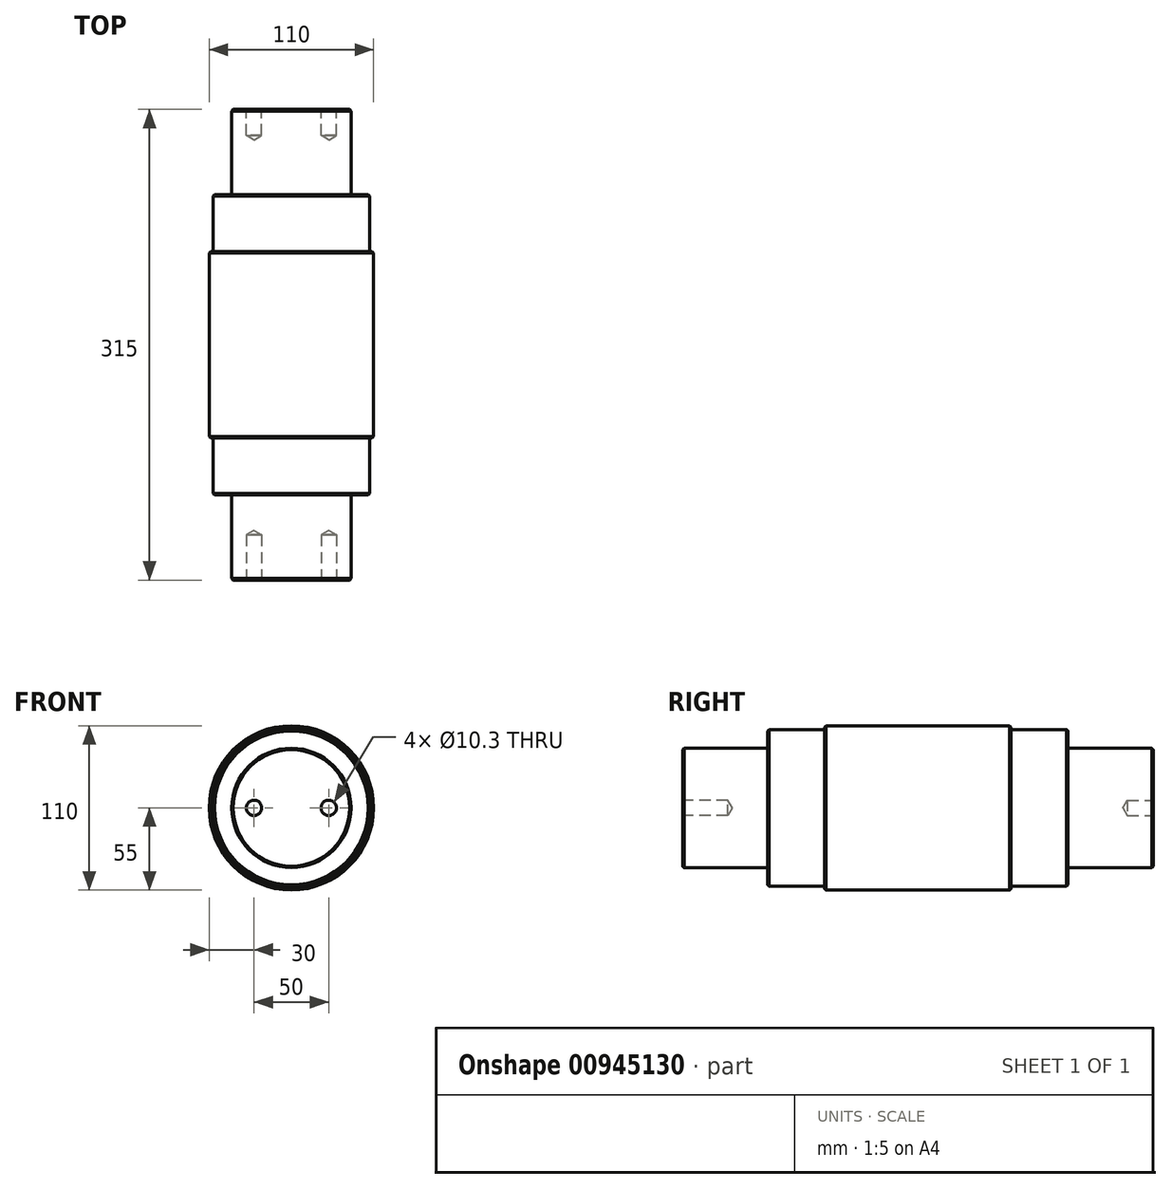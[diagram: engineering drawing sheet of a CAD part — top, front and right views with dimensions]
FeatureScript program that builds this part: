
annotation { "Feature Type Name" : "Feature", "Feature Type Description" : "" }
export const myFeature = defineFeature(function(context is Context, id is Id, definition is map)
    precondition{}
    {
        {
            var Q0;
            Q0=qCreatedBy(makeId("Front.planeOp"),FACE);
            var sketch = newSketch(context, id + "F0", { "sketchPlane" : qUnion([Q0])});
            skCircle(sketch, "E0", {"center": v(0, 0) * mm, "radius": 55 * mm});
            skSolve(sketch);
        }
        {
            var Q0;
            Q0=makeQuery(id+"F0.imprint","IMPRINT",FACE,{"disambiguationData":[TD([[makeQuery(id+"F0.imprint","IMPRINT",EDGE,{"derivedFrom":sQuery(id+"F0.wireOp",EDGE,"E0")}),1.0]])]});
            extrude(context, id + "F1", {"entities" : qUnion([Q0]), "oppositeDirection" : true, "depth" : 125 * mm, "offsetDistance" : 25 * mm});
        }
        {
            var Q0;
            Q0=makeQuery(id+"F1.opExtrude","CAP_FACE",FACE,{"disambiguationData":[OSD([sQuery(id+"F0.wireOp",EDGE,"E0")])],"isStart":true});
            var sketch = newSketch(context, id + "F2", { "sketchPlane" : qUnion([Q0])});
            skCircle(sketch, "E1", {"center": v(0, 0) * mm, "radius": 52.5 * mm});
            skSolve(sketch);
        }
        {
            var Q0;
            Q0=makeQuery(id+"F2.imprint","IMPRINT",FACE,{"disambiguationData":[TD([[makeQuery(id+"F2.imprint","IMPRINT",EDGE,{"derivedFrom":sQuery(id+"F2.wireOp",EDGE,"E1")}),1.0]])]});
            extrude(context, id + "F3", {"entities" : qUnion([Q0]), "operationType" : NewBodyOperationType.ADD, "depth" : 38 * mm, "offsetDistance" : 25 * mm});
        }
        {
            var Q0;
            Q0=makeQuery(id+"F3.opExtrude","CAP_FACE",FACE,{"disambiguationData":[OSD([sQuery(id+"F2.wireOp",EDGE,"E1")])],"isStart":false});
            var sketch = newSketch(context, id + "F4", { "sketchPlane" : qUnion([Q0])});
            skCircle(sketch, "E2", {"center": v(0, 0) * mm, "radius": 40 * mm});
            skSolve(sketch);
        }
        {
            var Q0;
            Q0=makeQuery(id+"F4.imprint","IMPRINT",FACE,{"disambiguationData":[TD([[makeQuery(id+"F4.imprint","IMPRINT",EDGE,{"derivedFrom":sQuery(id+"F4.wireOp",EDGE,"E2")}),1.0]])]});
            extrude(context, id + "F5", {"entities" : qUnion([Q0]), "operationType" : NewBodyOperationType.ADD, "depth" : 57 * mm, "offsetDistance" : 25 * mm});
        }
        {
            var Q0;
            Q0=makeQuery(id+"F1.opExtrude","CAP_FACE",FACE,{"disambiguationData":[OSD([sQuery(id+"F0.wireOp",EDGE,"E0")])],"isStart":false});
            var sketch = newSketch(context, id + "F6", { "sketchPlane" : qUnion([Q0])});
            skCircle(sketch, "E3", {"center": v(0, 0) * mm, "radius": 52.5 * mm});
            skSolve(sketch);
        }
        {
            var Q0;
            Q0=makeQuery(id+"F6.imprint","IMPRINT",FACE,{"disambiguationData":[TD([[makeQuery(id+"F6.imprint","IMPRINT",EDGE,{"derivedFrom":sQuery(id+"F6.wireOp",EDGE,"E3")}),1.0]])]});
            extrude(context, id + "F7", {"entities" : qUnion([Q0]), "operationType" : NewBodyOperationType.ADD, "depth" : 38 * mm, "offsetDistance" : 25 * mm});
        }
        {
            var Q0;
            Q0=makeQuery(id+"F7.opExtrude","CAP_FACE",FACE,{"disambiguationData":[OSD([sQuery(id+"F6.wireOp",EDGE,"E3")])],"isStart":false});
            var sketch = newSketch(context, id + "F8", { "sketchPlane" : qUnion([Q0])});
            skCircle(sketch, "E4", {"center": v(0, 0) * mm, "radius": 40 * mm});
            skSolve(sketch);
        }
        {
            var Q0;
            Q0=makeQuery(id+"F8.imprint","IMPRINT",FACE,{"disambiguationData":[TD([[makeQuery(id+"F8.imprint","IMPRINT",EDGE,{"derivedFrom":sQuery(id+"F8.wireOp",EDGE,"E4")}),1.0]])]});
            extrude(context, id + "F9", {"entities" : qUnion([Q0]), "operationType" : NewBodyOperationType.ADD, "depth" : 57 * mm, "offsetDistance" : 25 * mm});
        }
        {
            var Q0;
            Q0=makeQuery(id+"F5.opExtrude","CAP_EDGE",EDGE,{"disambiguationData":[OSD([sQuery(id+"F4.wireOp",EDGE,"E2")])],"isStart":false});
            chamfer(context, id + "F10", {"entities" : qUnion([Q0]), "width" : 1 * mm, "tangentPropagation" : true});
        }
        {
            var Q0;
            Q0=makeQuery(id+"F3.opExtrude","CAP_EDGE",EDGE,{"disambiguationData":[OSD([sQuery(id+"F2.wireOp",EDGE,"E1")])],"isStart":false});
            chamfer(context, id + "F11", {"entities" : qUnion([Q0]), "width" : 1 * mm, "tangentPropagation" : true});
        }
        {
            var Q0;
            Q0=makeQuery(id+"F1.opExtrude","CAP_EDGE",EDGE,{"disambiguationData":[OSD([sQuery(id+"F0.wireOp",EDGE,"E0")])],"isStart":true});
            chamfer(context, id + "F12", {"entities" : qUnion([Q0]), "width" : 1 * mm, "tangentPropagation" : true});
        }
        {
            var Q0;
            Q0=makeQuery(id+"F9.opExtrude","CAP_EDGE",EDGE,{"disambiguationData":[OSD([sQuery(id+"F8.wireOp",EDGE,"E4")])],"isStart":false});
            chamfer(context, id + "F13", {"entities" : qUnion([Q0]), "width" : 1 * mm, "tangentPropagation" : true});
        }
        {
            var Q0;
            Q0=makeQuery(id+"F7.opExtrude","CAP_EDGE",EDGE,{"disambiguationData":[OSD([sQuery(id+"F6.wireOp",EDGE,"E3")])],"isStart":false});
            chamfer(context, id + "F14", {"entities" : qUnion([Q0]), "width" : 1 * mm, "tangentPropagation" : true});
        }
        {
            var Q0;
            Q0=makeQuery(id+"F1.opExtrude","CAP_EDGE",EDGE,{"disambiguationData":[OSD([sQuery(id+"F0.wireOp",EDGE,"E0")])],"isStart":false});
            chamfer(context, id + "F15", {"entities" : qUnion([Q0]), "width" : 1 * mm, "tangentPropagation" : true});
        }
        {
            var Q0;
            Q0=makeQuery(id+"F5.opExtrude","CAP_FACE",FACE,{"disambiguationData":[OSD([sQuery(id+"F4.wireOp",EDGE,"E2")])],"isStart":false});
            var sketch = newSketch(context, id + "F16", { "sketchPlane" : qUnion([Q0])});
            skLineSegment(sketch, "E5", {"start": v(0, 0) * mm, "end": v(25, 0) * mm, "construction": true});
            skLineSegment(sketch, "E6", {"start": v(0, 0) * mm, "end": v(-25, 0) * mm, "construction": true});
            skSolve(sketch);
        }
        {
            var Q0;
            Q0=sQuery(id+"F16.wireOp",VERTEX,"E6.end");
            var Q1;
            Q1=sQuery(id+"F16.wireOp",VERTEX,"E5.end");
            var Q2;
            Q2=makeQuery(id+"F1.opExtrude","SWEPT_BODY",BODY,{"disambiguationData":[OSD([sQuery(id+"F0.wireOp",EDGE,"E0")])]});
            hole(context, id + "F17", {"style" : HoleStyle.SIMPLE, "endStyle" : HoleEndStyle.BLIND, "standardTappedOrClearance" : lookupTablePath({ "standard" : "ISO", "engagement" : "75%", "pitch" : "1.75 mm", "size" : "M12", "type" : "Tapped" }), "standardBlindInLast" : lookupTablePath({ "standard" : "ISO", "fit" : "Normal", "engagement" : "75%", "pitch" : "1.75 mm", "size" : "M12", "type" : "Clearance & tapped" }), "holeDiameter" : 10.3 * mm, "majorDiameter" : 12 * mm, "showTappedDepth" : true, "holeDepth" : 30.25 * mm, "isTappedThrough" : true, "tappedDepth" : 25 * mm, "tapClearance" : 3, "startFromSketch" : true, "locations" : qUnion([Q0, Q1]), "scope" : qUnion([Q2])});
        }
        {
            var Q0;
            Q0=makeQuery(id+"F9.opExtrude","CAP_FACE",FACE,{"disambiguationData":[OSD([sQuery(id+"F8.wireOp",EDGE,"E4")])],"isStart":false});
            var sketch = newSketch(context, id + "F18", { "sketchPlane" : qUnion([Q0])});
            skLineSegment(sketch, "E7", {"start": v(0, 0) * mm, "end": v(25, 0) * mm, "construction": true});
            skLineSegment(sketch, "E8", {"start": v(0, 0) * mm, "end": v(-25, 0) * mm, "construction": true});
            skSolve(sketch);
        }
        {
            var Q0;
            Q0=sQuery(id+"F18.wireOp",VERTEX,"E8.end");
            var Q1;
            Q1=sQuery(id+"F18.wireOp",VERTEX,"E7.end");
            var Q2;
            Q2=makeQuery(id+"F1.opExtrude","SWEPT_BODY",BODY,{"disambiguationData":[OSD([sQuery(id+"F0.wireOp",EDGE,"E0")])]});
            hole(context, id + "F19", {"style" : HoleStyle.SIMPLE, "endStyle" : HoleEndStyle.BLIND, "standardTappedOrClearance" : lookupTablePath({ "standard" : "ISO", "engagement" : "75%", "pitch" : "1.75 mm", "size" : "M12", "type" : "Tapped" }), "standardBlindInLast" : lookupTablePath({ "standard" : "ISO", "fit" : "Normal", "engagement" : "75%", "pitch" : "1.75 mm", "size" : "M12", "type" : "Clearance & tapped" }), "holeDiameter" : 10.3 * mm, "majorDiameter" : 12 * mm, "showTappedDepth" : true, "holeDepth" : 17.25 * mm, "isTappedThrough" : true, "tappedDepth" : 12 * mm, "tapClearance" : 3, "startFromSketch" : true, "locations" : qUnion([Q0, Q1]), "scope" : qUnion([Q2])});
        }
    });
